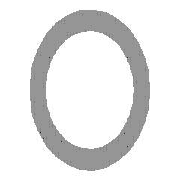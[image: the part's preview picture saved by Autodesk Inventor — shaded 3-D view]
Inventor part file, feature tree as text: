
AUTODESK INVENTOR PART (.ipt)
format: ipt  version: 2025 (Build 290162010, 162A)  size: 121,344 bytes
history: native  units: mm (DEFAULTED — no unit token found)
features: other x3, sketch x1, plane x1
ambient origin geometry x8: Origin, YZ Plane, XZ Plane, XY Plane, X Axis, Y Axis, Z Axis, Center Point
bodies: Solid1 (feature_tree), Body (feature_tree)
feature tree (5):
  other  "Driven Length"
  other  "Start plane"
  other  "End plane"
  sketch  "Sketch3"  dims[d0=168.3mm d1=2.0mm d2=650.0mm d3=0.0mm d4=-0.0mm d5=650.0mm d6=90.0deg d7=650.0mm]
  plane  "Work Plane3"
